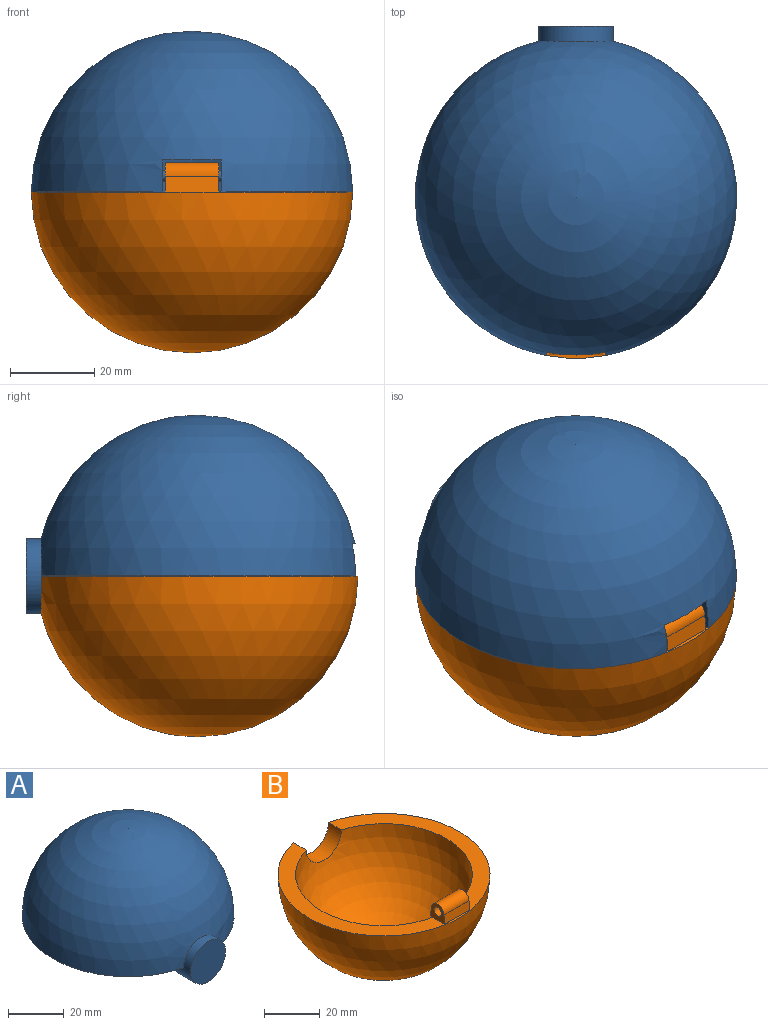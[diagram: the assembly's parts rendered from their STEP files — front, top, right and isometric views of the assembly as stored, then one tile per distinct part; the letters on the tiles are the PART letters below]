
ASSEMBLY  parts=2 mates=1
PART A: 11 faces, bbox 76.2x78.7x47 mm
  f0: sphere r=38.1mm, area 8887.2mm2, adj f1,f3,f4,f7,f8,f9
  f1: plane 74.5x38.1mm, normal (0,0,-1), area 598.7mm2, adj f0,f2,f4,f5,f9
  f2: sphere r=31.75mm, area 6225.5mm2, adj f1,f3,f7,f8,f9
  f3: plane 74.5x38.1mm, normal (0,0,-1), area 598.7mm2, adj f0,f2,f4,f5,f8
  f4: cylinder r=8.89mm len=17.78mm, axis (0,1,0), area 348.6mm2, adj f0,f1,f3,f5,f6
  f5: plane 17.78x8.89mm, normal (0,1,0), area 124.1mm2, adj f1,f3,f4
  f6: plane 17.78x17.78mm, normal (0,-1,0), area 248.3mm2, adj f4
  f7: plane 13.97x7.31mm, normal (0,0,-1), area 91.6mm2, adj f0,f2,f8,f9
  f8: plane 7.61x7.43mm, normal (1,0,0), area 44.7mm2, adj f0,f2,f3,f7,f10
  f9: plane 7.61x7.43mm, normal (-1,0,0), area 44.7mm2, adj f0,f1,f2,f7,f10
  f10: cylinder r=1.27mm len=13.97mm, axis (1,0,0), area 111.5mm2, adj f8,f9
PART B: 11 faces, bbox 76.2x76.2x45.1 mm
  f0: sphere r=31.75mm, area 6207.2mm2, adj f1,f3,f4
  f1: plane 76.2x75.15mm, normal (0,0,1), area 1206.5mm2, adj f0,f2,f3,f8,f9,f10
  f2: sphere r=38.1mm, area 8994.9mm2, adj f1,f3
  f3: cylinder r=8.89mm len=17.78mm, axis (0,-1,0), area 183.4mm2, adj f0,f1,f2
  f4: plane 12.7x1.81mm, normal (0,0,-1), area 20.2mm2, adj f0,f5,f9,f10
  f5: plane 12.7x4.37mm, normal (0,0.99,0.13), area 55.9mm2, adj f4,f6,f9,f10
  f6: cylinder r=3.17mm len=12.7mm, axis (-1,0,0), area 120.4mm2, adj f5,f8,f9,f10
  f7: cylinder r=1.91mm len=12.7mm, axis (-1,0,0), area 152mm2, adj f9,f10
  f8: plane 12.7x3.74mm, normal (0,-0.99,0.12), area 47.9mm2, adj f1,f6,f9,f10
  f9: plane 7.33x6.99mm, normal (1,0,0), area 30.5mm2, adj f1,f4,f5,f6,f7,f8
  f10: plane 7.33x6.99mm, normal (-1,0,0), area 30.5mm2, adj f1,f4,f5,f6,f7,f8
PLACE A rot(axis=(0,0,1),180deg) t=(0,0,0)mm
PLACE B at identity
MATE revolute A.f10 <-> B.f6  axis (-1,0,0) through (0,-33.65,3.81)mm
